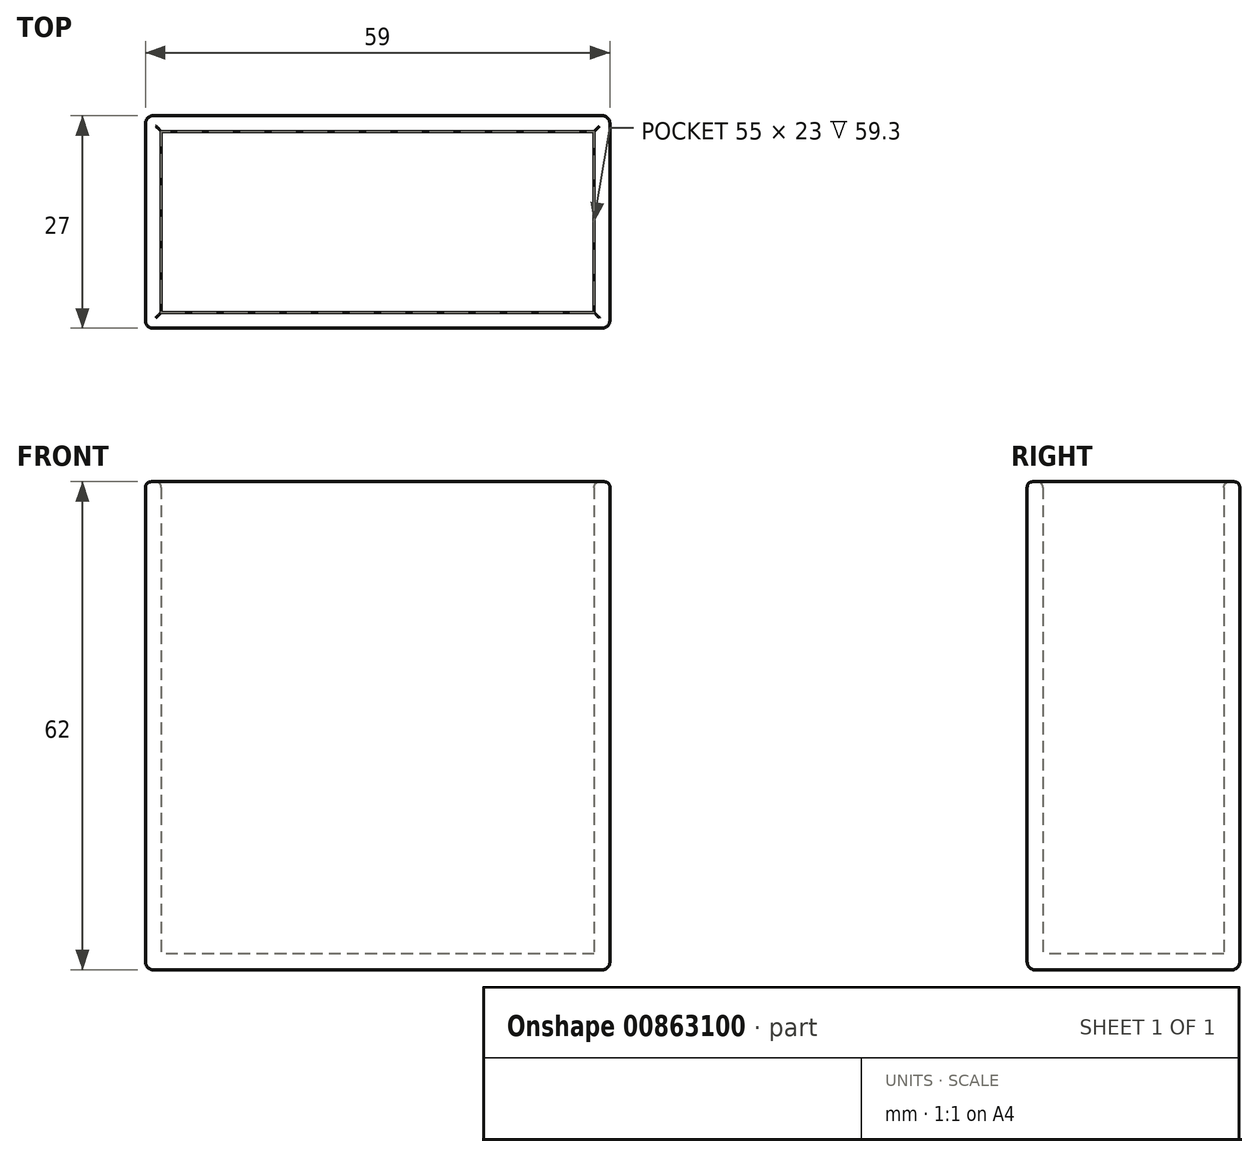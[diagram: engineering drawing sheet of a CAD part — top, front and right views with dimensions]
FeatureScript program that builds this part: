
annotation { "Feature Type Name" : "Feature", "Feature Type Description" : "" }
export const myFeature = defineFeature(function(context is Context, id is Id, definition is map)
    precondition{}
    {
        {
            var Q0;
            Q0=qCreatedBy(makeId("Top.planeOp"),FACE);
            var sketch = newSketch(context, id + "F0", { "sketchPlane" : qUnion([Q0])});
            skLineSegment(sketch, "E0.bottom", {"start": v(27.5, 11.5) * mm, "end": v(-27.5, 11.5) * mm});
            skLineSegment(sketch, "E0.top", {"start": v(27.5, -11.5) * mm, "end": v(-27.5, -11.5) * mm});
            skLineSegment(sketch, "E0.left", {"start": v(27.5, 11.5) * mm, "end": v(27.5, -11.5) * mm});
            skLineSegment(sketch, "E0.right", {"start": v(-27.5, 11.5) * mm, "end": v(-27.5, -11.5) * mm});
            skPoint(sketch, "E0.middle", {"position": v(0, 0) * mm});
            skSolve(sketch);
        }
        {
            var Q0;
            Q0 = qSketchRegion(id + "F0", true);
            extrude(context, id + "F1", {"entities" : qUnion([Q0]), "depth" : 60 * mm, "offsetDistance" : 25 * mm});
        }
        {
            var Q0;
            Q0=makeQuery(id+"F1.opExtrude","CAP_FACE",FACE,{"disambiguationData":[OSD([sQuery(id+"F0.wireOp",EDGE,"E0.bottom"),sQuery(id+"F0.wireOp",EDGE,"E0.top"),sQuery(id+"F0.wireOp",EDGE,"E0.left"),sQuery(id+"F0.wireOp",EDGE,"E0.right")])],"isStart":false});
            shell(context, id + "F2", {"entities" : qUnion([Q0]), "thickness" : 2 * mm, "oppositeDirection" : true});
        }
        {
            var Q0;
            Q0=makeQuery(id+"F1.opExtrude","CAP_EDGE",EDGE,{"disambiguationData":[OSD([sQuery(id+"F0.wireOp",EDGE,"E0.right")])],"isStart":true});
            var Q1;
            Q1=makeQuery(id+"F1.opExtrude","CAP_EDGE",EDGE,{"disambiguationData":[OSD([sQuery(id+"F0.wireOp",EDGE,"E0.bottom")])],"isStart":true});
            var Q2;
            Q2=makeQuery(id+"F1.opExtrude","CAP_EDGE",EDGE,{"disambiguationData":[OSD([sQuery(id+"F0.wireOp",EDGE,"E0.top")])],"isStart":true});
            var Q3;
            Q3=makeQuery(id+"F1.opExtrude","CAP_EDGE",EDGE,{"disambiguationData":[OSD([sQuery(id+"F0.wireOp",EDGE,"E0.left")])],"isStart":true});
            var Q4;
            Q4=makeQuery(id+"F1.opExtrude","SWEPT_EDGE",EDGE,{"disambiguationData":[OSD([sQuery(id+"F0.wireOp",EDGE,"E0.top"),sQuery(id+"F0.wireOp",EDGE,"E0.left")])]});
            var Q5;
            Q5=makeQuery(id+"F1.opExtrude","SWEPT_EDGE",EDGE,{"disambiguationData":[OSD([sQuery(id+"F0.wireOp",EDGE,"E0.bottom"),sQuery(id+"F0.wireOp",EDGE,"E0.left")])]});
            var Q6;
            Q6=makeQuery(id+"F1.opExtrude","SWEPT_EDGE",EDGE,{"disambiguationData":[OSD([sQuery(id+"F0.wireOp",EDGE,"E0.bottom"),sQuery(id+"F0.wireOp",EDGE,"E0.right")])]});
            var Q7;
            Q7=makeQuery(id+"F1.opExtrude","SWEPT_EDGE",EDGE,{"disambiguationData":[OSD([sQuery(id+"F0.wireOp",EDGE,"E0.top"),sQuery(id+"F0.wireOp",EDGE,"E0.right")])]});
            fillet(context, id + "F3", {"entities" : qUnion([Q0, Q1, Q2, Q3, Q4, Q5, Q6, Q7]), "radius" : 1 * mm, "tangentPropagation" : true, "allowEdgeOverflow" : false});
        }
        {
            var Q0;
            Q0=makeQuery(id+"F1.opExtrude","CAP_EDGE",EDGE,{"disambiguationData":[OSD([sQuery(id+"F0.wireOp",EDGE,"E0.top")])],"isStart":false});
            var Q1;
            Q1=makeQuery(id+"F1.opExtrude","CAP_EDGE",EDGE,{"disambiguationData":[OSD([sQuery(id+"F0.wireOp",EDGE,"E0.left")])],"isStart":false});
            var Q2;
            Q2=makeQuery(id+"F1.opExtrude","CAP_EDGE",EDGE,{"disambiguationData":[OSD([sQuery(id+"F0.wireOp",EDGE,"E0.bottom")])],"isStart":false});
            var Q3;
            Q3=makeQuery(id+"F1.opExtrude","CAP_EDGE",EDGE,{"disambiguationData":[OSD([sQuery(id+"F0.wireOp",EDGE,"E0.right")])],"isStart":false});
            var Q4;
            {var subQ0=sQuery(id+"F0.wireOp",EDGE,"E0.bottom");Q4=makeQuery(id+"F2.opShell","OFFSET_EDGE",EDGE,{"disambiguationData":[OSD([subQ0]),TDD([makeQuery(id+"F1.opExtrude","CAP_EDGE",EDGE,{"disambiguationData":[OSD([subQ0])],"isStart":false})])]});}
            var Q5;
            {var subQ0=sQuery(id+"F0.wireOp",EDGE,"E0.top");Q5=makeQuery(id+"F2.opShell","OFFSET_EDGE",EDGE,{"disambiguationData":[OSD([subQ0]),TDD([makeQuery(id+"F1.opExtrude","CAP_EDGE",EDGE,{"disambiguationData":[OSD([subQ0])],"isStart":false})])]});}
            var Q6;
            {var subQ0=sQuery(id+"F0.wireOp",EDGE,"E0.right");Q6=makeQuery(id+"F2.opShell","OFFSET_EDGE",EDGE,{"disambiguationData":[OSD([subQ0]),TDD([makeQuery(id+"F1.opExtrude","CAP_EDGE",EDGE,{"disambiguationData":[OSD([subQ0])],"isStart":false})])]});}
            var Q7;
            {var subQ0=sQuery(id+"F0.wireOp",EDGE,"E0.left");Q7=makeQuery(id+"F2.opShell","OFFSET_EDGE",EDGE,{"disambiguationData":[OSD([subQ0]),TDD([makeQuery(id+"F1.opExtrude","CAP_EDGE",EDGE,{"disambiguationData":[OSD([subQ0])],"isStart":false})])]});}
            fillet(context, id + "F4", {"entities" : qUnion([Q0, Q1, Q2, Q3, Q4, Q5, Q6, Q7]), "radius" : 0.7 * mm, "tangentPropagation" : true, "allowEdgeOverflow" : false});
        }
    });
